# Revit family: for update_75417CHN_new
name_source: partatom
category: Plumbing Fixtures
revit_build: Autodesk Revit 2018 (Build: 20170223_1515(x64)
units: mm (PartAtom-declared; Revit-internal decimal feet)

## family parameters
Always vertical = No
Cut with Voids When Loaded = No
OmniClass Number = 23.31.11.00
OmniClass Title = Faucets
Part Type = Normal
Room Calculation Point = No
Round Connector Dimension = Use Diameter
Shared = No
Work Plane-Based = Yes

## types (5) — shared parameters
Always visible = Yes
BIMobject category = Taps & Mixers
Default Elevation = 1219.2 mm  [stored 4 ft]
Description = DuoTurn E Mixer for concealed installation for 2 functions
Design country = Germany
Edition number = 1
IFC Classification = Valve
Manufacturer = Hansgrohe
Manufacturer country = Germany
Manufacturer name = hansgrohe
Masterformat 2014 Code = 22 41 39
Masterformat 2014 Description = Residential Faucets, Supplies, and Trim
Model = 75417CHN
OmniClass Code = 23-31 11 00
OmniClass Description = Faucets
Product Guid = 229ccd39-7df7-4ee9-bb6b-19e21ad63f8f
Product SKU = 75417CHN
Product data url = https://bimobject.com
Product name = 75417CHN DuoTurn E Mixer for concealed installation for 2 functions
Product url = https://www.hansgrohe.com
QR code = https://bimobject.com
UNSPSC Code = 301815
URL = https://www.hansgrohe.com
Uniclass 2015 Code = Pr_40_20_87
Uniclass 2015 Name = Taps and water supply outlet fittings
Uniformat II Code = D2010
Uniformat II Description = Plumbing Fixtures
Weight Net (Kg) = 2.2

## per-type parameters (varying)
| type | Material 1 |
| 707 Matte White | Hansgrohe - Metal - 707 Matte White |
| 677 Matte Black | Hansgrohe - Metal - 677 Matte Black |
| 007 Chrome | Hansgrohe - Metal - 007 Chrome |
| 147 Brushed Bronze | Hansgrohe - Metal - 147 Brushed Bronze |
| 997 Polished Gold Optic | Hansgrohe - Metal - 997 Polished Gold Optic |

note: [stored X ft] marks values corroborated as IEEE doubles in the binary element streams (Revit-internal decimal feet)

## geometry (parser evidence)
native form markers: Sweep x2
no freeform markers — native parametric forms only
